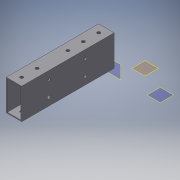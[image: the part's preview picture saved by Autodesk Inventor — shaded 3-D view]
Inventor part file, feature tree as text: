
AUTODESK INVENTOR PART (.ipt)
format: ipt  version: 2018 (Build 220112000, 112)  size: 171,008 bytes
history: native  units: in
note: dims shown in document units (in); Inventor stores cm internally (conversion verified against a paired STEP export)
features: plane x4, extrude x4, sketch x4
ambient origin geometry x8: Origin, YZ Plane, XZ Plane, XY Plane, X Axis, Y Axis, Z Axis, Center Point
bodies: Body1 (feature_tree)
feature tree (12):
  plane  "Work Plane1"
  extrude  "Extrusion16"  TaperAngle=0.0deg  [1 undecoded]
  plane  "Work Plane4"
  extrude  "Extrusion17"  Depth=6.0in
  plane  "Work Plane3"
  extrude  "Extrusion22"  Depth=0.5in
  plane  "Work Plane2"
  extrude  "Extrusion23"  Depth=2.0in
  sketch  "Sketch20"  dims[d71=1.0in d72=2.0in d73=0.065in d74=0.065in d75=0.065in d76=0.065in d77=0.1in d78=0.0in]
  sketch  "Sketch21"  dims[d79=6.0in d80=0.0in d81=0.5in]
  sketch  "Sketch26"  dims[d82=0.5in d83=0.5in]
  sketch  "Sketch27"  dims[d84=1.0in d85=0.5in d86=0.2031in d87=0.2031in d88=0.2031in d89=1.0in d90=1.0in d91=1.0in d92=0.2031in d93=0.2031in d94=0.5in d95=0.5in d96=3.0in d97=0.0in d122=0.2031in d123=1.765in d124=0.5in d125=0.2031in d126=2.355in d129=1.0in d130=0.2031in d131=1.0in d132=0.2031in d133=1.0in d134=0.0in d135=0.5in d136=0.5in d137=1.5in d138=0.5in d139=0.2031in d140=0.2031in d141=2.0in d142=0.0in d143=0.5in]
note: 1 required parameter value undecoded (feature->parameter linkage not recoverable at this tier; creation-order binding heuristic only, values carry confidence <= 0.55)
